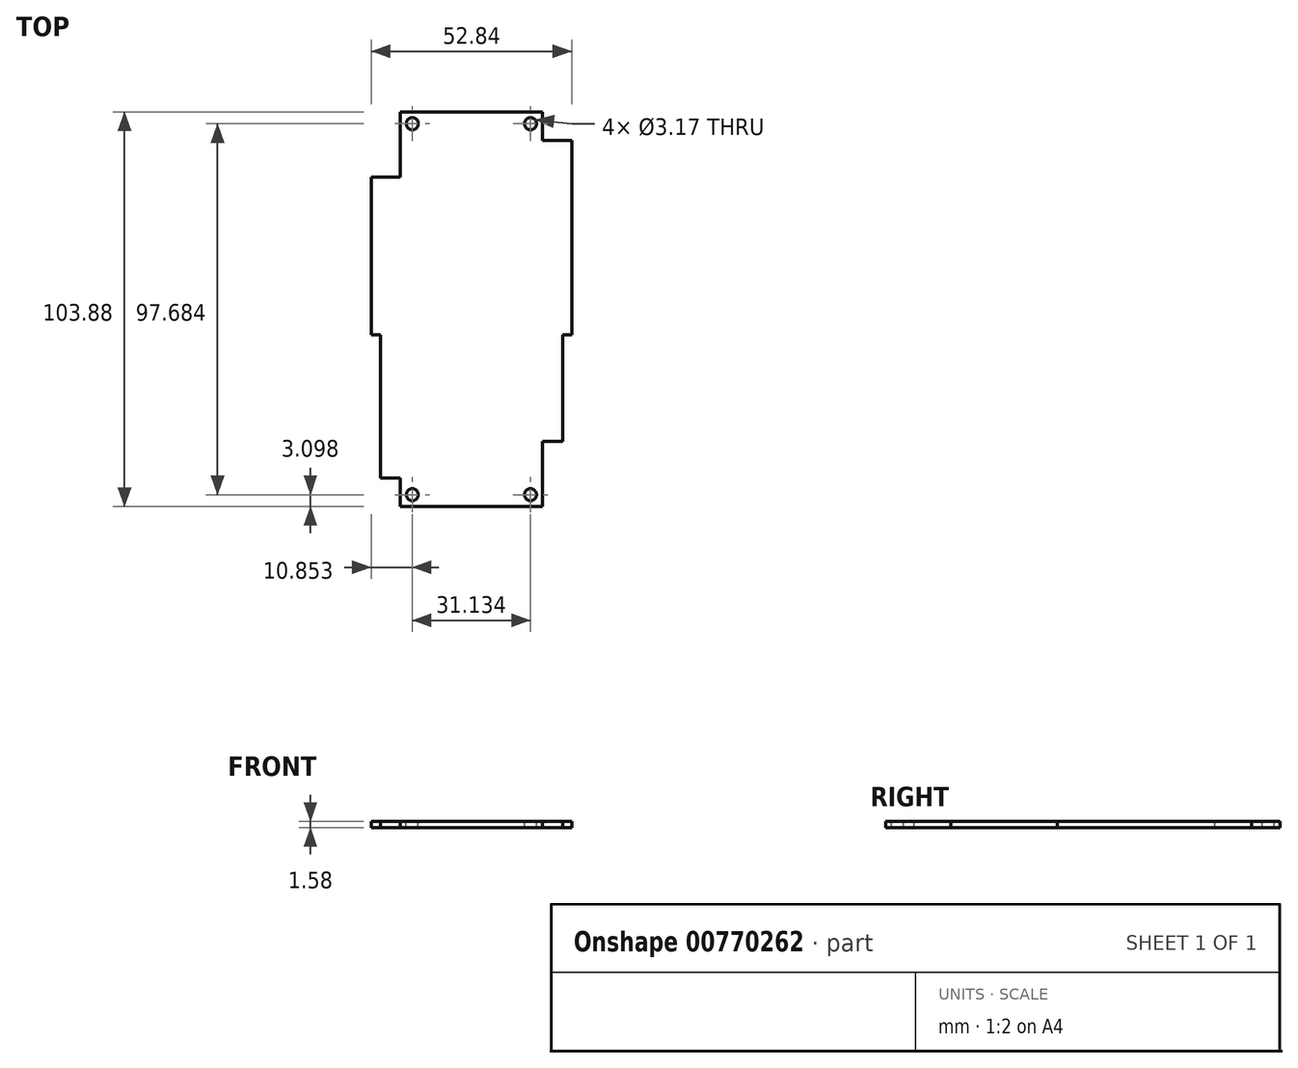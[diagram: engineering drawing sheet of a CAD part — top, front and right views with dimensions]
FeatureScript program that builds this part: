
annotation { "Feature Type Name" : "Feature", "Feature Type Description" : "" }
export const myFeature = defineFeature(function(context is Context, id is Id, definition is map)
    precondition{}
    {
        {
            var Q0;
            Q0=qCreatedBy(makeId("Top.planeOp"),FACE);
            var sketch = newSketch(context, id + "F0", { "sketchPlane" : qUnion([Q0])});
            skLineSegment(sketch, "E0.bottom", {"start": v(26.42, 51.94) * mm, "end": v(-26.42, 51.94) * mm});
            skLineSegment(sketch, "E0.top", {"start": v(26.42, -51.94) * mm, "end": v(-26.42, -51.94) * mm});
            skLineSegment(sketch, "E0.left", {"start": v(26.42, 51.94) * mm, "end": v(26.42, -51.94) * mm});
            skLineSegment(sketch, "E0.right", {"start": v(-26.42, 51.94) * mm, "end": v(-26.42, -51.94) * mm});
            skPoint(sketch, "E0.middle", {"position": v(0, 0) * mm});
            skSolve(sketch);
        }
        {
            var Q0;
            Q0=makeQuery(id+"F0.imprint","IMPRINT",FACE,{"disambiguationData":[TD([[makeQuery(id+"F0.imprint","IMPRINT",EDGE,{"derivedFrom":sQuery(id+"F0.wireOp",EDGE,"E0.bottom")}),1.0]])]});
            extrude(context, id + "F1", {"entities" : qUnion([Q0]), "endBound" : BoundingType.SYMMETRIC, "depth" : 1.59 * mm});
        }
        {
            var Q0;
            Q0=makeQuery(id+"F1.opExtrude","CAP_FACE",FACE,{"disambiguationData":[OSD([sQuery(id+"F0.wireOp",EDGE,"E0.bottom"),sQuery(id+"F0.wireOp",EDGE,"E0.top"),sQuery(id+"F0.wireOp",EDGE,"E0.left"),sQuery(id+"F0.wireOp",EDGE,"E0.right")])],"isStart":false});
            var sketch = newSketch(context, id + "F2", { "sketchPlane" : qUnion([Q0])});
            skLineSegment(sketch, "E1.bottom", {"start": v(-26.42, 51.94) * mm, "end": v(-18.77, 51.94) * mm});
            skLineSegment(sketch, "E1.top", {"start": v(-26.42, 34.77) * mm, "end": v(-18.77, 34.77) * mm});
            skLineSegment(sketch, "E1.left", {"start": v(-26.42, 51.94) * mm, "end": v(-26.42, 34.77) * mm});
            skLineSegment(sketch, "E1.right", {"start": v(-18.77, 51.94) * mm, "end": v(-18.77, 34.77) * mm});
            skLineSegment(sketch, "E2.bottom", {"start": v(26.42, 51.94) * mm, "end": v(18.77, 51.94) * mm});
            skLineSegment(sketch, "E2.top", {"start": v(26.42, 44.42) * mm, "end": v(18.77, 44.42) * mm});
            skLineSegment(sketch, "E2.left", {"start": v(26.42, 51.94) * mm, "end": v(26.42, 44.42) * mm});
            skLineSegment(sketch, "E2.right", {"start": v(18.77, 51.94) * mm, "end": v(18.77, 44.42) * mm});
            skLineSegment(sketch, "E3.bottom", {"start": v(-26.42, -51.94) * mm, "end": v(-18.77, -51.94) * mm});
            skLineSegment(sketch, "E3.top", {"start": v(-26.42, -44.42) * mm, "end": v(-18.77, -44.42) * mm});
            skLineSegment(sketch, "E3.left", {"start": v(-26.42, -51.94) * mm, "end": v(-26.42, -44.42) * mm});
            skLineSegment(sketch, "E3.right", {"start": v(-18.77, -51.94) * mm, "end": v(-18.77, -44.42) * mm});
            skLineSegment(sketch, "E4.bottom", {"start": v(-26.42, -44.42) * mm, "end": v(-24.01, -44.42) * mm});
            skLineSegment(sketch, "E4.top", {"start": v(-26.42, -6.7) * mm, "end": v(-24.01, -6.7) * mm});
            skLineSegment(sketch, "E4.left", {"start": v(-26.42, -44.42) * mm, "end": v(-26.42, -6.7) * mm});
            skLineSegment(sketch, "E4.right", {"start": v(-24.01, -44.42) * mm, "end": v(-24.01, -6.7) * mm});
            skLineSegment(sketch, "E5.bottom", {"start": v(26.42, -51.94) * mm, "end": v(18.77, -51.94) * mm});
            skLineSegment(sketch, "E5.top", {"start": v(26.42, -34.77) * mm, "end": v(18.77, -34.77) * mm});
            skLineSegment(sketch, "E5.left", {"start": v(26.42, -51.94) * mm, "end": v(26.42, -34.77) * mm});
            skLineSegment(sketch, "E5.right", {"start": v(18.77, -51.94) * mm, "end": v(18.77, -34.77) * mm});
            skLineSegment(sketch, "E6.bottom", {"start": v(26.42, -34.77) * mm, "end": v(24, -34.77) * mm});
            skLineSegment(sketch, "E6.top", {"start": v(26.42, -6.7) * mm, "end": v(24, -6.7) * mm});
            skLineSegment(sketch, "E6.left", {"start": v(26.42, -34.77) * mm, "end": v(26.42, -6.7) * mm});
            skLineSegment(sketch, "E6.right", {"start": v(24, -34.77) * mm, "end": v(24, -6.7) * mm});
            skCircle(sketch, "E7", {"center": v(-15.57, 48.84) * mm, "radius": 1.59 * mm});
            skCircle(sketch, "E8.MirrorC", {"center": v(15.57, 48.84) * mm, "radius": 1.59 * mm});
            skCircle(sketch, "E9.MirrorC", {"center": v(-15.57, -48.84) * mm, "radius": 1.59 * mm});
            skCircle(sketch, "E10.MirrorC", {"center": v(15.57, -48.84) * mm, "radius": 1.59 * mm});
            skSolve(sketch);
        }
        {
            var Q0;
            Q0=qSketchRegion(id+"F2",true);
            extrude(context, id + "F3", {"entities" : qUnion([Q0]), "operationType" : NewBodyOperationType.REMOVE, "oppositeDirection" : true, "depth" : 1.6 * mm});
        }
    });
